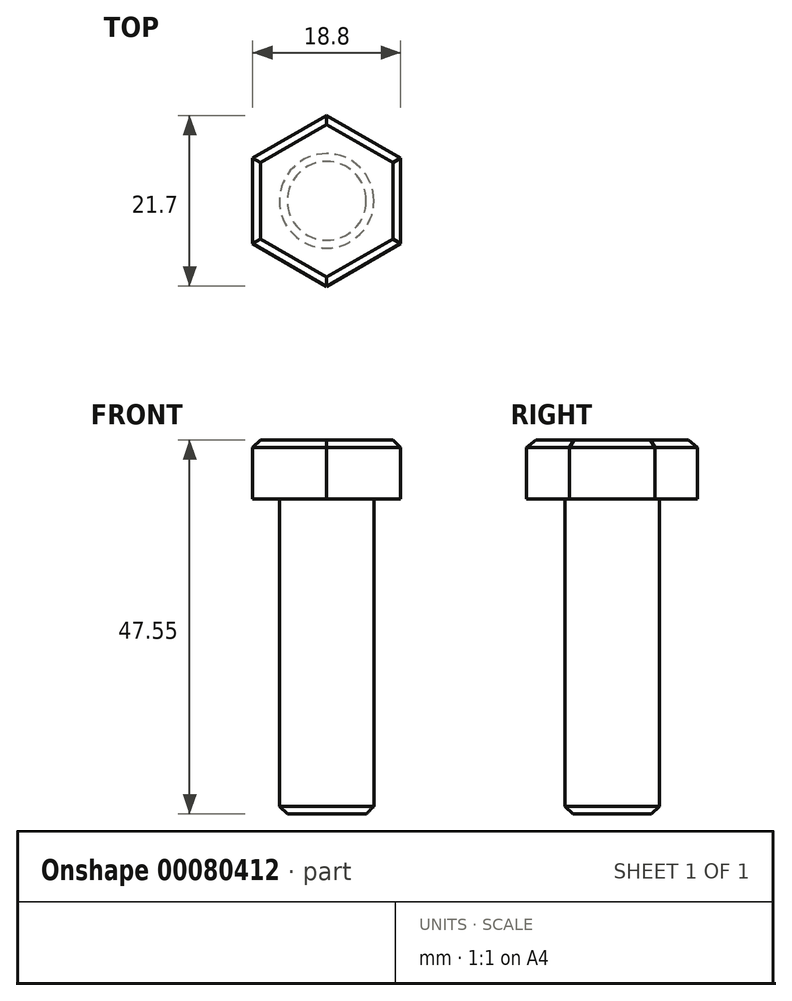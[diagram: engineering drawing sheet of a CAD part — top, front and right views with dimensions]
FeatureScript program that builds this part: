
annotation { "Feature Type Name" : "Feature", "Feature Type Description" : "" }
export const myFeature = defineFeature(function(context is Context, id is Id, definition is map)
    precondition{}
    {
        {
            var Q0;
            Q0=qCreatedBy(makeId("Top.planeOp"),FACE);
            var sketch = newSketch(context, id + "F0", { "sketchPlane" : qUnion([Q0])});
            skCircle(sketch, "E0", {"center": v(0, 0) * mm, "radius": 6 * mm});
            skSolve(sketch);
        }
        {
            var Q0;
            Q0 = qSketchRegion(id + "F0", true);
            extrude(context, id + "F1", {"entities" : qUnion([Q0]), "endBound" : BoundingType.SYMMETRIC, "depth" : 40 * mm});
        }
        {
            var Q0;
            Q0=makeQuery(id+"F1.opExtrude","CAP_FACE",FACE,{"disambiguationData":[OSD([sQuery(id+"F0.wireOp",EDGE,"E0")])],"isStart":false});
            var sketch = newSketch(context, id + "F2", { "sketchPlane" : qUnion([Q0])});
            skCircle(sketch, "E1.cCircle", {"center": v(0, 0) * mm, "radius": 9.4 * mm, "construction": true});
            skLineSegment(sketch, "E1.0", {"start": v(-9.4, 5.43) * mm, "end": v(0, 10.85) * mm});
            skLineSegment(sketch, "E1.1", {"start": v(0, 10.85) * mm, "end": v(9.4, 5.43) * mm});
            skLineSegment(sketch, "E1.2", {"start": v(9.4, 5.43) * mm, "end": v(9.4, -5.43) * mm});
            skLineSegment(sketch, "E1.3", {"start": v(9.4, -5.43) * mm, "end": v(0, -10.85) * mm});
            skLineSegment(sketch, "E1.4", {"start": v(0, -10.85) * mm, "end": v(-9.4, -5.43) * mm});
            skLineSegment(sketch, "E1.5", {"start": v(-9.4, -5.43) * mm, "end": v(-9.4, 5.43) * mm});
            skPoint(sketch, "E1.0.midPoint", {"position": v(-4.7, 8.14) * mm});
            skSolve(sketch);
        }
        {
            var Q0;
            Q0 = qSketchRegion(id + "F2", true);
            extrude(context, id + "F3", {"entities" : qUnion([Q0]), "operationType" : NewBodyOperationType.ADD, "depth" : 7.55 * mm});
        }
        {
            var Q0;
            Q0=makeQuery(id+"F1.opExtrude","CAP_EDGE",EDGE,{"disambiguationData":[OSD([sQuery(id+"F0.wireOp",EDGE,"E0")])],"isStart":true});
            chamfer(context, id + "F4", {"entities" : qUnion([Q0]), "width" : 1 * mm, "tangentPropagation" : true});
        }
        {
            var Q0;
            Q0=makeQuery(id+"F3.opExtrude","CAP_FACE",FACE,{"disambiguationData":[OSD([sQuery(id+"F2.wireOp",EDGE,"E1.0"),sQuery(id+"F2.wireOp",EDGE,"E1.1"),sQuery(id+"F2.wireOp",EDGE,"E1.2"),sQuery(id+"F2.wireOp",EDGE,"E1.3"),sQuery(id+"F2.wireOp",EDGE,"E1.4"),sQuery(id+"F2.wireOp",EDGE,"E1.5")])],"isStart":false});
            chamfer(context, id + "F5", {"entities" : qUnion([Q0]), "width" : 1 * mm, "tangentPropagation" : true});
        }
    });
